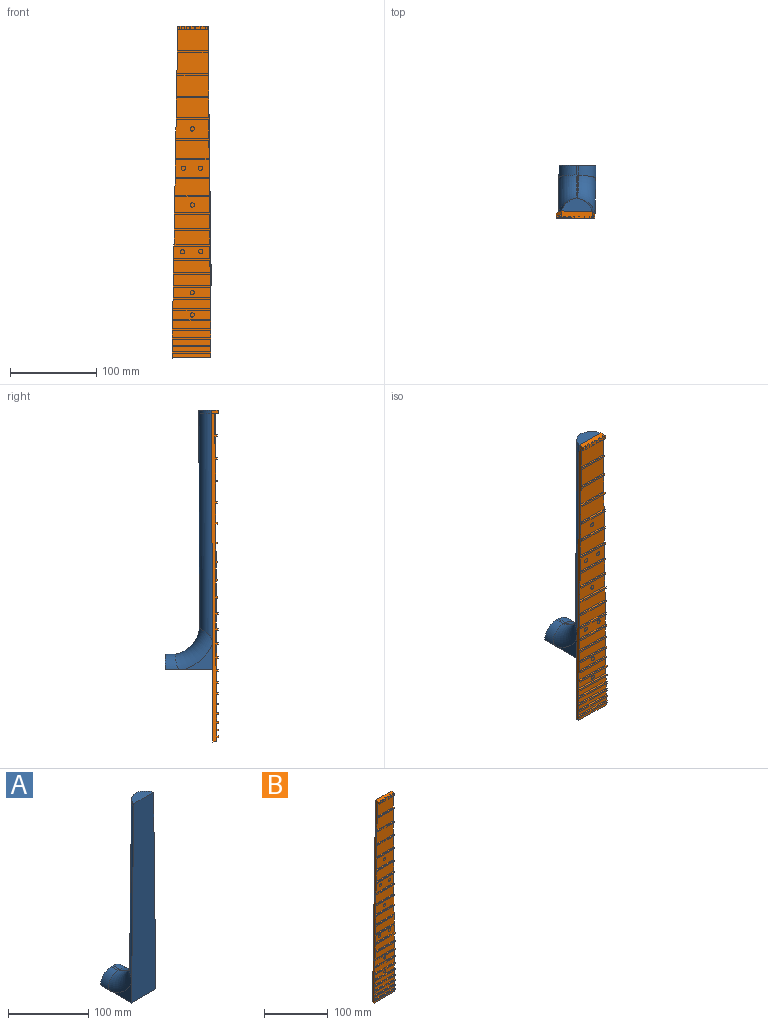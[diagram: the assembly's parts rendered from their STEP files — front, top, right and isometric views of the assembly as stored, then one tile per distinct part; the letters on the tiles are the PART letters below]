
ASSEMBLY  parts=2 mates=1
PART A: 20 faces, bbox 43x64.5x307.5 mm
  f0: cylinder r=34.84mm len=31.87mm, axis (-1,0,0.01), area 61.3mm2, adj f1,f2,f3,f4,f10,f13
  f1: plane 11.52x3.01mm, normal (0,0,1), area 33.8mm2, adj f0,f3,f8,f10,f12,f13,f14,f16
  f2: plane 4.55x0.63mm, normal (1,0,-0.01), area 0mm2, adj f0,f4,f10,f16
  f3: plane 18.82x9.84mm, normal (1,0,-0.01), area 0.5mm2, adj f0,f1,f10
  f4: plane 105.54x2.83mm, normal (0,1,0), area 145.3mm2, adj f0,f2,f13,f15,f16,f18
  f5: plane 35x14.91mm, normal (0,0,1), area 374.6mm2, adj f6,f17,f19
  f6: plane 301.5x42.8mm, normal (0,-1,0), area 11712.5mm2, adj f5,f7,f9,f11,f15,f17,f18,f19
  f7: plane 55x42.8mm, normal (0,0,-1), area 2353.9mm2, adj f6,f8,f9,f11,f12,f14
  f8: plane 42.8x18mm, normal (0,1,0), area 602.4mm2, adj f1,f7,f12,f14
  f9: plane 34.27x29.54mm, normal (-1,0,0.01), area 357.5mm2, adj f6,f7,f13
  f10: cylinder r=34.99mm len=31.4mm, axis (1,0,0.01), area 30.1mm2, adj f0,f1,f2,f3,f16
  f11: plane 34.1x29.54mm, normal (1,0,0.01), area 356.7mm2, adj f6,f7,f16
  f12: cylinder r=20mm len=20.73mm, axis (0,-1,0), area 365.4mm2, adj f1,f7,f8,f13
  f13: torus R=54.84mm, axis (-1,0,0.01), area 1561.3mm2, adj f0,f1,f4,f9,f12,f15
  f14: cylinder r=20mm len=20.9mm, axis (0,1,0), area 375.7mm2, adj f1,f7,f8,f16
  f15: cylinder r=20mm len=268.33mm, axis (0.01,0,1), area 6531.6mm2, adj f4,f6,f13,f17,f18
  f16: torus R=54.99mm, axis (1,0,0.01), area 1550.2mm2, adj f1,f2,f4,f10,f11,f14,f18
  f17: cylinder r=20mm len=17.5mm, axis (0,0,-1), area 99.4mm2, adj f5,f6,f15,f19
  f18: cylinder r=20mm len=268.33mm, axis (0.01,0,-1), area 6532.4mm2, adj f4,f6,f15,f16,f19
  f19: cylinder r=20mm len=17.5mm, axis (0,0,-1), area 99.4mm2, adj f5,f6,f17,f18
PART B: 134 faces, bbox 45x8x385.5 mm
  f0: plane 381.5x6.6mm, normal (-1,0,0.02), area 1610.2mm2, adj f1,f3,f4,f5,f6,f16,f36,f37
  f1: plane 45x4mm, normal (0,0,-1), area 180mm2, adj f0,f2,f3,f4
  f2: plane 381.5x6mm, normal (1,0,0.01), area 1610.1mm2, adj f1,f3,f4,f5,f6,f34,f36,f37
  f3: plane 45x5mm, normal (0,-1,0), area 224.7mm2, adj f0,f1,f2,f5
  f4: plane 385.5x45mm, normal (0,1,0), area 15438.9mm2, adj f0,f1,f2,f8,f16,f34
  f5: plane 44.87x2mm, normal (0,0,-1), area 89.7mm2, adj f0,f2,f3,f87
  f6: plane 35.84x25mm, normal (0,-1,0), area 888mm2, adj f0,f2,f7,f36
  f7: plane 35.2x4mm, normal (0,0,-1), area 129.4mm2, adj f6,f9,f10,f11,f12,f13,f14,f15
  f8: plane 35.2x8mm, normal (0,0,1), area 270.2mm2, adj f4,f9,f10,f11,f12,f13,f14,f15
  f9: plane 4x1.5mm, normal (0,-1,0), area 6mm2, adj f7,f8,f15,f19
  f10: plane 4x1.3mm, normal (0,-1,0), area 5.2mm2, adj f7,f8,f18,f22
  f11: plane 4x1mm, normal (0,-1,0), area 4mm2, adj f7,f8,f21,f25
  f12: plane 4x0.8mm, normal (0,-1,0), area 3.2mm2, adj f7,f8,f24,f28
  f13: plane 4x0.6mm, normal (0,-1,0), area 2.4mm2, adj f7,f8,f27,f31
  f14: plane 4x0.5mm, normal (0,-1,0), area 2mm2, adj f7,f8,f30,f33
  f15: plane 4x2mm, normal (1,0,0), area 8mm2, adj f7,f8,f9,f17
  f16: plane 8x4mm, normal (-1,0,0), area 32mm2, adj f0,f4,f7,f8,f17
  f17: plane 4x2.5mm, normal (0,-1,0), area 10mm2, adj f7,f8,f15,f16
  f18: plane 4x2mm, normal (1,0,0), area 8mm2, adj f7,f8,f10,f20
  f19: plane 4x2mm, normal (-1,0,0), area 8mm2, adj f7,f8,f9,f20
  f20: plane 4.5x4mm, normal (0,-1,0), area 18mm2, adj f7,f8,f18,f19
  f21: plane 4x2mm, normal (1,0,0), area 8mm2, adj f7,f8,f11,f23
  f22: plane 4x2mm, normal (-1,0,0), area 8mm2, adj f7,f8,f10,f23
  f23: plane 4.5x4mm, normal (0,-1,0), area 18mm2, adj f7,f8,f21,f22
  f24: plane 4x2mm, normal (1,0,0), area 8mm2, adj f7,f8,f12,f26
  f25: plane 4x2mm, normal (-1,0,0), area 8mm2, adj f7,f8,f11,f26
  f26: plane 4.5x4mm, normal (0,-1,0), area 18mm2, adj f7,f8,f24,f25
  f27: plane 4x2mm, normal (1,0,0), area 8mm2, adj f7,f8,f13,f29
  f28: plane 4x2mm, normal (-1,0,0), area 8mm2, adj f7,f8,f12,f29
  f29: plane 5.5x4mm, normal (0,-1,0), area 22mm2, adj f7,f8,f27,f28
  f30: plane 4x2mm, normal (1,0,0), area 8mm2, adj f7,f8,f14,f32
  f31: plane 4x2mm, normal (-1,0,0.01), area 8mm2, adj f7,f8,f13,f32
  f32: plane 5.52x4mm, normal (0,-1,0), area 22.1mm2, adj f7,f8,f30,f31
  f33: plane 4x2mm, normal (-1,0,0), area 8mm2, adj f7,f8,f14,f35
  f34: plane 8x4mm, normal (1,0,0), area 32mm2, adj f2,f4,f7,f8,f35
  f35: plane 4x2.5mm, normal (0,-1,0), area 10mm2, adj f7,f8,f33,f34
  f36: plane 35.84x2mm, normal (0,0,1), area 71.7mm2, adj f0,f2,f6,f133
  f37: plane 36.52x24.5mm, normal (0,-1,0), area 887.1mm2, adj f0,f2,f38,f132
  f38: plane 36.52x2mm, normal (0,0,1), area 73mm2, adj f0,f2,f37,f131
  f39: plane 37.19x24mm, normal (0,-1,0), area 885.2mm2, adj f0,f2,f40,f130
  f40: plane 37.19x2mm, normal (0,0,1), area 74.4mm2, adj f0,f2,f39,f129
  f41: plane 37.83x23mm, normal (0,-1,0), area 863.4mm2, adj f0,f2,f42,f128
  f42: plane 37.83x2mm, normal (0,0,1), area 75.7mm2, adj f0,f2,f41,f126
  f43: cylinder r=2.5mm len=5mm, axis (0,1,0), area 1.6mm2, adj f44,f127
  f44: plane 38.45x22mm, normal (0,-1,0), area 820mm2, adj f0,f2,f43,f45,f125
  f45: plane 38.45x2mm, normal (0,0,1), area 76.9mm2, adj f0,f2,f44,f124
  f46: plane 39.04x21mm, normal (0,-1,0), area 814.2mm2, adj f0,f2,f47,f123
  f47: plane 39.04x2mm, normal (0,0,1), area 78.1mm2, adj f0,f2,f46,f120
  f48: cylinder r=2.5mm len=5mm, axis (0,1,0), area 1.6mm2, adj f50,f121
  f49: cylinder r=2.5mm len=5mm, axis (0,1,0), area 1.6mm2, adj f50,f122
  f50: plane 39.61x20mm, normal (0,-1,0), area 747.7mm2, adj f0,f2,f48,f49,f51,f119
  f51: plane 39.61x2mm, normal (0,0,1), area 79.2mm2, adj f0,f2,f50,f118
  f52: plane 40.15x19mm, normal (0,-1,0), area 758.1mm2, adj f0,f2,f53,f117
  f53: plane 40.15x2mm, normal (0,0,1), area 80.3mm2, adj f0,f2,f52,f115
  f54: cylinder r=2.5mm len=5mm, axis (0,1,0), area 1.6mm2, adj f55,f116
  f55: plane 40.66x18mm, normal (0,-1,0), area 708.1mm2, adj f0,f2,f54,f56,f114
  f56: plane 40.66x2mm, normal (0,0,1), area 81.3mm2, adj f0,f2,f55,f113
  f57: plane 41.15x17mm, normal (0,-1,0), area 695.8mm2, adj f0,f2,f58,f112
  f58: plane 41.15x2mm, normal (0,0,1), area 82.3mm2, adj f0,f2,f57,f111
  f59: plane 41.61x16mm, normal (0,-1,0), area 662.5mm2, adj f0,f2,f60,f110
  f60: plane 41.61x2mm, normal (0,0,1), area 83.2mm2, adj f0,f2,f59,f107
  f61: cylinder r=2.5mm len=5mm, axis (0,1,0), area 1.6mm2, adj f63,f109
  f62: cylinder r=2.5mm len=5mm, axis (0,1,0), area 1.6mm2, adj f63,f108
  f63: plane 42.05x15mm, normal (0,-1,0), area 588.5mm2, adj f0,f2,f61,f62,f64,f106
  f64: plane 42.05x2mm, normal (0,0,1), area 84.1mm2, adj f0,f2,f63,f105
  f65: plane 42.46x14mm, normal (0,-1,0), area 591.9mm2, adj f0,f2,f66,f104
  f66: plane 42.46x2mm, normal (0,0,1), area 84.9mm2, adj f0,f2,f65,f103
  f67: plane 42.84x13mm, normal (0,-1,0), area 554.8mm2, adj f0,f2,f68,f102
  f68: plane 42.84x2mm, normal (0,0,1), area 85.7mm2, adj f0,f2,f67,f100
  f69: cylinder r=2.5mm len=5mm, axis (0,1,0), area 1.6mm2, adj f70,f101
  f70: plane 43.2x12mm, normal (0,-1,0), area 496.9mm2, adj f0,f2,f69,f71,f99
  f71: plane 43.2x2mm, normal (0,0,1), area 86.4mm2, adj f0,f2,f70,f98
  f72: plane 43.54x11mm, normal (0,-1,0), area 477.3mm2, adj f0,f2,f73,f97
  f73: plane 43.54x2mm, normal (0,0,1), area 87.1mm2, adj f0,f2,f72,f95
  f74: cylinder r=2.5mm len=5mm, axis (0,1,0), area 1.6mm2, adj f75,f96
  f75: plane 43.84x10mm, normal (0,-1,0), area 417.5mm2, adj f0,f2,f74,f76,f94
  f76: plane 43.84x2mm, normal (0,0,1), area 87.7mm2, adj f0,f2,f75,f93
  f77: plane 44.13x9mm, normal (0,-1,0), area 396.1mm2, adj f0,f2,f78,f92
  f78: plane 44.13x2mm, normal (0,0,1), area 88.3mm2, adj f0,f2,f77,f91
  f79: plane 44.38x8mm, normal (0,-1,0), area 354.2mm2, adj f0,f2,f80,f90
  f80: plane 44.38x2mm, normal (0,0,1), area 88.8mm2, adj f0,f2,f79,f89
  f81: plane 44.61x7mm, normal (0,-1,0), area 311.7mm2, adj f0,f2,f82,f88
  f82: plane 44.61x2mm, normal (0,0,1), area 89.2mm2, adj f0,f2,f81,f85
  f83: plane 44.82x6mm, normal (0,-1,0), area 268.5mm2, adj f0,f2,f84,f86
  f84: plane 44.67x2mm, normal (0,0,-1), area 89.3mm2, adj f0,f2,f83,f85
  f85: plane 44.67x2mm, normal (0,-1,0), area 89.3mm2, adj f0,f2,f82,f84
  f86: plane 44.82x2mm, normal (0,0,1), area 89.6mm2, adj f0,f2,f83,f87
  f87: plane 44.87x2mm, normal (0,-1,0), area 89.7mm2, adj f0,f2,f5,f86
  f88: plane 44.44x2mm, normal (0,0,-1), area 88.9mm2, adj f0,f2,f81,f89
  f89: plane 44.44x2mm, normal (0,-1,0), area 88.8mm2, adj f0,f2,f80,f88
  f90: plane 44.18x2mm, normal (0,0,-1), area 88.4mm2, adj f0,f2,f79,f91
  f91: plane 44.18x2mm, normal (0,-1,0), area 88.3mm2, adj f0,f2,f78,f90
  f92: plane 43.9x2mm, normal (0,0,-1), area 87.8mm2, adj f0,f2,f77,f93
  f93: plane 43.9x2mm, normal (0,-1,0), area 87.7mm2, adj f0,f2,f76,f92
  f94: plane 43.59x2mm, normal (0,0,-1), area 87.2mm2, adj f0,f2,f75,f95
  f95: plane 43.59x2mm, normal (0,-1,0), area 87.1mm2, adj f0,f2,f73,f94
  f96: plane 5x5mm, normal (0,-1,0), area 19.6mm2, adj f74
  f97: plane 43.25x2mm, normal (0,0,-1), area 86.5mm2, adj f0,f2,f72,f98
  f98: plane 43.25x2mm, normal (0,-1,0), area 86.5mm2, adj f0,f2,f71,f97
  f99: plane 42.89x2mm, normal (0,0,-1), area 85.8mm2, adj f0,f2,f70,f100
  f100: plane 42.89x2mm, normal (0,-1,0), area 85.7mm2, adj f0,f2,f68,f99
  f101: plane 5x5mm, normal (0,-1,0), area 19.6mm2, adj f69
  f102: plane 42.51x2mm, normal (0,0,-1), area 85mm2, adj f0,f2,f67,f103
  f103: plane 42.51x2mm, normal (0,-1,0), area 85mm2, adj f0,f2,f66,f102
  f104: plane 42.1x2mm, normal (0,0,-1), area 84.2mm2, adj f0,f2,f65,f105
  f105: plane 42.1x2mm, normal (0,-1,0), area 84.1mm2, adj f0,f2,f64,f104
  f106: plane 41.66x2mm, normal (0,0,-1), area 83.3mm2, adj f0,f2,f63,f107
  f107: plane 41.66x2mm, normal (0,-1,0), area 83.3mm2, adj f0,f2,f60,f106
  f108: plane 5x5mm, normal (0,-1,0), area 19.6mm2, adj f62
  f109: plane 5x5mm, normal (0,-1,0), area 19.6mm2, adj f61
  f110: plane 41.2x2mm, normal (0,0,-1), area 82.4mm2, adj f0,f2,f59,f111
  f111: plane 41.2x2mm, normal (0,-1,0), area 82.3mm2, adj f0,f2,f58,f110
  f112: plane 40.71x2mm, normal (0,0,-1), area 81.4mm2, adj f0,f2,f57,f113
  f113: plane 40.71x2mm, normal (0,-1,0), area 81.4mm2, adj f0,f2,f56,f112
  f114: plane 40.2x2mm, normal (0,0,-1), area 80.4mm2, adj f0,f2,f55,f115
  f115: plane 40.2x2mm, normal (0,-1,0), area 80.3mm2, adj f0,f2,f53,f114
  f116: plane 5x5mm, normal (0,-1,0), area 19.6mm2, adj f54
  f117: plane 39.66x2mm, normal (0,0,-1), area 79.3mm2, adj f0,f2,f52,f118
  f118: plane 39.66x2mm, normal (0,-1,0), area 79.3mm2, adj f0,f2,f51,f117
  f119: plane 39.09x2mm, normal (0,0,-1), area 78.2mm2, adj f0,f2,f50,f120
  f120: plane 39.09x2mm, normal (0,-1,0), area 78.1mm2, adj f0,f2,f47,f119
  f121: plane 5x5mm, normal (0,-1,0), area 19.6mm2, adj f48
  f122: plane 5x5mm, normal (0,-1,0), area 19.6mm2, adj f49
  f123: plane 38.5x2mm, normal (0,0,-1), area 77mm2, adj f0,f2,f46,f124
  f124: plane 38.5x2mm, normal (0,-1,0), area 77mm2, adj f0,f2,f45,f123
  f125: plane 37.88x2mm, normal (0,0,-1), area 75.8mm2, adj f0,f2,f44,f126
  f126: plane 37.88x2mm, normal (0,-1,0), area 75.7mm2, adj f0,f2,f42,f125
  f127: plane 5x5mm, normal (0,-1,0), area 19.6mm2, adj f43
  f128: plane 37.24x2mm, normal (0,0,-1), area 74.5mm2, adj f0,f2,f41,f129
  f129: plane 37.24x2mm, normal (0,-1,0), area 74.4mm2, adj f0,f2,f40,f128
  f130: plane 36.57x2mm, normal (0,0,-1), area 73.1mm2, adj f0,f2,f39,f131
  f131: plane 36.57x2mm, normal (0,-1,0), area 73.1mm2, adj f0,f2,f38,f130
  f132: plane 35.89x2mm, normal (0,0,-1), area 71.8mm2, adj f0,f2,f37,f133
  f133: plane 35.89x2mm, normal (0,-1,0), area 71.7mm2, adj f0,f2,f36,f132
PLACE A rot(axis=(-0.29,0,-0.96),0.9deg) t=(29.62,390.7,-7.51)mm
PLACE B rot(axis=(-0.29,0,-0.96),0.9deg) t=(-139.82,393.36,-1.44)mm fixed
MATE fastened A.f5 <-> B.f8  axis (0,0,1) through (-156.62,394.55,193.3)mm
